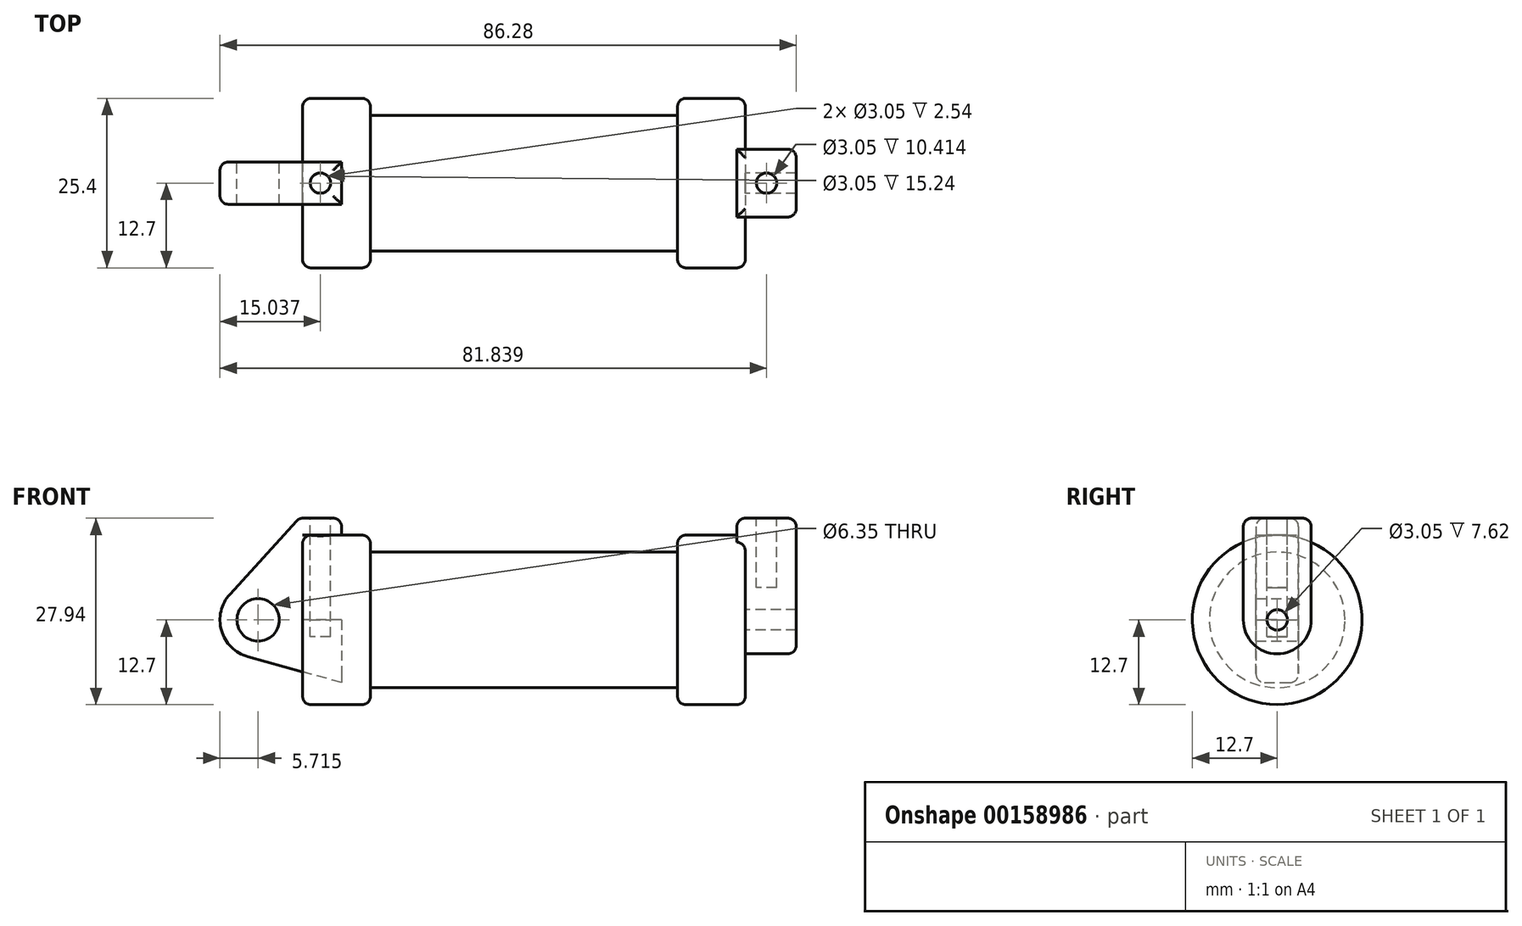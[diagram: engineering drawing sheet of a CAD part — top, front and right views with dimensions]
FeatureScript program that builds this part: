
annotation { "Feature Type Name" : "Feature", "Feature Type Description" : "" }
export const myFeature = defineFeature(function(context is Context, id is Id, definition is map)
    precondition{}
    {
        {
            var Q0;
            Q0=qCreatedBy(makeId("Front.planeOp"),FACE);
            var sketch = newSketch(context, id + "F0", { "sketchPlane" : qUnion([Q0])});
            skLineSegment(sketch, "E0", {"start": v(0, 0) * mm, "end": v(0, 12.7) * mm});
            skLineSegment(sketch, "E1", {"start": v(0, 12.7) * mm, "end": v(10.16, 12.7) * mm});
            skLineSegment(sketch, "E2", {"start": v(10.16, 12.7) * mm, "end": v(10.16, 10.16) * mm});
            skLineSegment(sketch, "E3", {"start": v(10.16, 10.16) * mm, "end": v(56.13, 10.16) * mm});
            skLineSegment(sketch, "E4", {"start": v(56.13, 10.16) * mm, "end": v(56.13, 12.7) * mm});
            skLineSegment(sketch, "E5", {"start": v(56.13, 12.7) * mm, "end": v(66.3, 12.7) * mm});
            skLineSegment(sketch, "E6", {"start": v(66.3, 12.7) * mm, "end": v(66.3, 0) * mm});
            skLineSegment(sketch, "E7", {"start": v(66.3, 0) * mm, "end": v(0, 0) * mm});
            skLineSegment(sketch, "E8", {"start": v(5.84, 15.24) * mm, "end": v(-0.5, 15.24) * mm});
            skLineSegment(sketch, "E9", {"start": v(-0.5, 15.24) * mm, "end": v(-10.88, 3.85) * mm});
            skLineSegment(sketch, "E10", {"start": v(0, 0) * mm, "end": v(-6.65, 0) * mm});
            skCircle(sketch, "E11", {"center": v(-6.65, 0) * mm, "radius": 5.72 * mm});
            skCircle(sketch, "E12", {"center": v(-6.65, 0) * mm, "radius": 3.18 * mm});
            skLineSegment(sketch, "E13", {"start": v(5.84, 15.24) * mm, "end": v(5.84, -9.4) * mm});
            skLineSegment(sketch, "E14", {"start": v(5.84, -9.4) * mm, "end": v(-8.18, -5.5) * mm});
            skSolve(sketch);
        }
        {
            var Q0;
            {var subQ0=sQuery(id+"F0.wireOp",EDGE,"E2");Q0=makeQuery(id+"F0.imprint","IMPRINT",FACE,{"disambiguationData":[TD([[makeQuery(id+"F0.imprint","IMPRINT",EDGE,{"derivedFrom":subQ0}),-1.0]])]});}
            var Q1;
            {var subQ0=sQuery(id+"F0.wireOp",EDGE,"E0");Q1=makeQuery(id+"F0.imprint","IMPRINT",FACE,{"disambiguationData":[TD([[makeQuery(id+"F0.imprint","IMPRINT",EDGE,{"derivedFrom":subQ0}),-1.0]])]});}
            var Q2;
            Q2=sQuery(id+"F0.wireOp",EDGE,"E7");
            revolve(context, id + "F1", {"entities" : qUnion([Q0, Q1]), "axis" : qUnion([Q2]), "revolveType" : RevolveType.FULL});
        }
        {
            var Q0;
            {var subQ4=sQuery(id+"F0.wireOp",EDGE,"E12");Q0=makeQuery(id+"F0.imprint","IMPRINT",FACE,{"disambiguationData":[TD([[makeQuery(id+"F0.imprint","IMPRINT",EDGE,{"derivedFrom":subQ4}),-1.0]])]});}
            var Q1;
            {var subQ3=sQuery(id+"F0.wireOp",EDGE,"E0");Q1=makeQuery(id+"F0.imprint","IMPRINT",FACE,{"disambiguationData":[TD([[makeQuery(id+"F0.imprint","IMPRINT",EDGE,{"derivedFrom":subQ3}),1.0]])]});}
            var Q2;
            {var subQ0=sQuery(id+"F0.wireOp",EDGE,"E14");Q2=makeQuery(id+"F0.imprint","IMPRINT",FACE,{"disambiguationData":[TD([[makeQuery(id+"F0.imprint","IMPRINT",EDGE,{"derivedFrom":subQ0}),-1.0]])]});}
            extrude(context, id + "F2", {"entities" : qUnion([Q0, Q1, Q2]), "endBound" : BoundingType.SYMMETRIC, "depth" : 6.35 * mm});
        }
        {
            var Q0;
            Q0=makeQuery(id+"F1.opRevolve","SWEPT_FACE",FACE,{"disambiguationData":[OSD([sQuery(id+"F0.wireOp",EDGE,"E6")])]});
            var sketch = newSketch(context, id + "F3", { "sketchPlane" : qUnion([Q0])});
            skPoint(sketch, "E15", {"position": v(0, 0) * mm});
            skCircle(sketch, "E16", {"center": v(0, 0) * mm, "radius": 1.52 * mm});
            skCircle(sketch, "E17", {"center": v(0, 0) * mm, "radius": 5.08 * mm});
            skLineSegment(sketch, "E18", {"start": v(-5.08, 0) * mm, "end": v(-5.08, 15.24) * mm});
            skLineSegment(sketch, "E19", {"start": v(5.08, 0) * mm, "end": v(5.08, 15.24) * mm});
            skLineSegment(sketch, "E20", {"start": v(5.08, 15.24) * mm, "end": v(-5.08, 15.24) * mm});
            skSolve(sketch);
        }
        {
            var Q0;
            Q0=qSketchRegion(id+"F3",true);
            extrude(context, id + "F4", {"entities" : qUnion([Q0]), "operationType" : NewBodyOperationType.ADD, "depth" : 7.62 * mm, "hasSecondDirection" : true, "secondDirectionOppositeDirection" : true, "secondDirectionDepth" : 1.27 * mm});
        }
        {
            var Q0;
            Q0=makeQuery(id+"F4.opExtrude","SWEPT_FACE",FACE,{"disambiguationData":[OSD([sQuery(id+"F3.wireOp",EDGE,"E20")])]});
            var sketch = newSketch(context, id + "F5", { "sketchPlane" : qUnion([Q0])});
            skCircle(sketch, "E21", {"center": v(69.47, 0) * mm, "radius": 1.52 * mm});
            skSolve(sketch);
        }
        {
            var Q0;
            Q0=qSketchRegion(id+"F5",true);
            extrude(context, id + "F6", {"entities" : qUnion([Q0]), "operationType" : NewBodyOperationType.REMOVE, "oppositeDirection" : true, "depth" : 10.4 * mm});
        }
        {
            var Q0;
            Q0=makeQuery(id+"F2.opExtrude","SWEPT_FACE",FACE,{"disambiguationData":[OSD([sQuery(id+"F0.wireOp",EDGE,"E8")])]});
            var sketch = newSketch(context, id + "F7", { "sketchPlane" : qUnion([Q0])});
            skCircle(sketch, "E22", {"center": v(2.67, 0) * mm, "radius": 1.52 * mm});
            skPoint(sketch, "E22.centerSnap0", {"position": v(2.67, 3.18) * mm});
            skPoint(sketch, "E22.centerSnap1", {"position": v(-0.5, 0) * mm});
            skSolve(sketch);
        }
        {
            var Q0;
            Q0=qSketchRegion(id+"F7",true);
            extrude(context, id + "F8", {"entities" : qUnion([Q0]), "operationType" : NewBodyOperationType.REMOVE, "oppositeDirection" : true, "depth" : 17.78 * mm});
        }
        {
            var Q0;
            Q0=makeQuery(id+"F2.opExtrude","CAP_EDGE",EDGE,{"disambiguationData":[OSD([sQuery(id+"F0.wireOp",EDGE,"E9")])],"isStart":true});
            var Q1;
            Q1=makeQuery(id+"F1.opRevolve","SWEPT_EDGE",EDGE,{"disambiguationData":[OSD([sQuery(id+"F0.wireOp",EDGE,"E0"),sQuery(id+"F0.wireOp",EDGE,"E1")])]});
            var Q2;
            Q2=makeQuery(id+"F2.opExtrude","CAP_EDGE",EDGE,{"disambiguationData":[OSD([sQuery(id+"F0.wireOp",EDGE,"E8")])],"isStart":true});
            var Q3;
            Q3=makeQuery(id+"F2.opExtrude","SWEPT_EDGE",EDGE,{"disambiguationData":[OSD([sQuery(id+"F0.wireOp",EDGE,"E8"),sQuery(id+"F0.wireOp",EDGE,"E9")])]});
            var Q4;
            Q4=makeQuery(id+"F2.opExtrude","CAP_EDGE",EDGE,{"disambiguationData":[OSD([sQuery(id+"F0.wireOp",EDGE,"E8")])],"isStart":false});
            var Q5;
            Q5=makeQuery(id+"F2.opExtrude","SWEPT_EDGE",EDGE,{"disambiguationData":[OSD([sQuery(id+"F0.wireOp",EDGE,"E8"),sQuery(id+"F0.wireOp",EDGE,"E13")])]});
            var Q6;
            Q6=makeQuery(id+"F2.opExtrude","CAP_EDGE",EDGE,{"disambiguationData":[OSD([sQuery(id+"F0.wireOp",EDGE,"E9")])],"isStart":false});
            var Q7;
            Q7=makeQuery(id+"F1.opRevolve","SWEPT_EDGE",EDGE,{"disambiguationData":[OSD([sQuery(id+"F0.wireOp",EDGE,"E1"),sQuery(id+"F0.wireOp",EDGE,"E2")])]});
            var Q8;
            Q8=makeQuery(id+"F1.opRevolve","SWEPT_EDGE",EDGE,{"disambiguationData":[OSD([sQuery(id+"F0.wireOp",EDGE,"E4"),sQuery(id+"F0.wireOp",EDGE,"E5")])]});
            var Q9;
            Q9=makeQuery(id+"F1.opRevolve","SWEPT_EDGE",EDGE,{"disambiguationData":[OSD([sQuery(id+"F0.wireOp",EDGE,"E5"),sQuery(id+"F0.wireOp",EDGE,"E6")])]});
            var Q10;
            Q10=makeQuery(id+"F4.opExtrude","SWEPT_EDGE",EDGE,{"disambiguationData":[OSD([sQuery(id+"F3.wireOp",EDGE,"E19"),sQuery(id+"F3.wireOp",EDGE,"E20")])]});
            var Q11;
            Q11=makeQuery(id+"F4.opExtrude","CAP_EDGE",EDGE,{"disambiguationData":[OSD([sQuery(id+"F3.wireOp",EDGE,"E20")])],"isStart":true});
            var Q12;
            Q12=makeQuery(id+"F4.opExtrude","CAP_EDGE",EDGE,{"disambiguationData":[OSD([sQuery(id+"F3.wireOp",EDGE,"E19")])],"isStart":false});
            var Q13;
            Q13=makeQuery(id+"F4.opExtrude","CAP_EDGE",EDGE,{"disambiguationData":[OSD([sQuery(id+"F3.wireOp",EDGE,"E20")])],"isStart":false});
            var Q14;
            Q14=makeQuery(id+"F4.opExtrude","SWEPT_EDGE",EDGE,{"disambiguationData":[OSD([sQuery(id+"F3.wireOp",EDGE,"E18"),sQuery(id+"F3.wireOp",EDGE,"E20")])]});
            fillet(context, id + "F9", {"entities" : qUnion([Q0, Q1, Q2, Q3, Q4, Q5, Q6, Q7, Q8, Q9, Q10, Q11, Q12, Q13, Q14]), "radius" : 1.27 * mm, "tangentPropagation" : true, "allowEdgeOverflow" : false});
        }
    });
